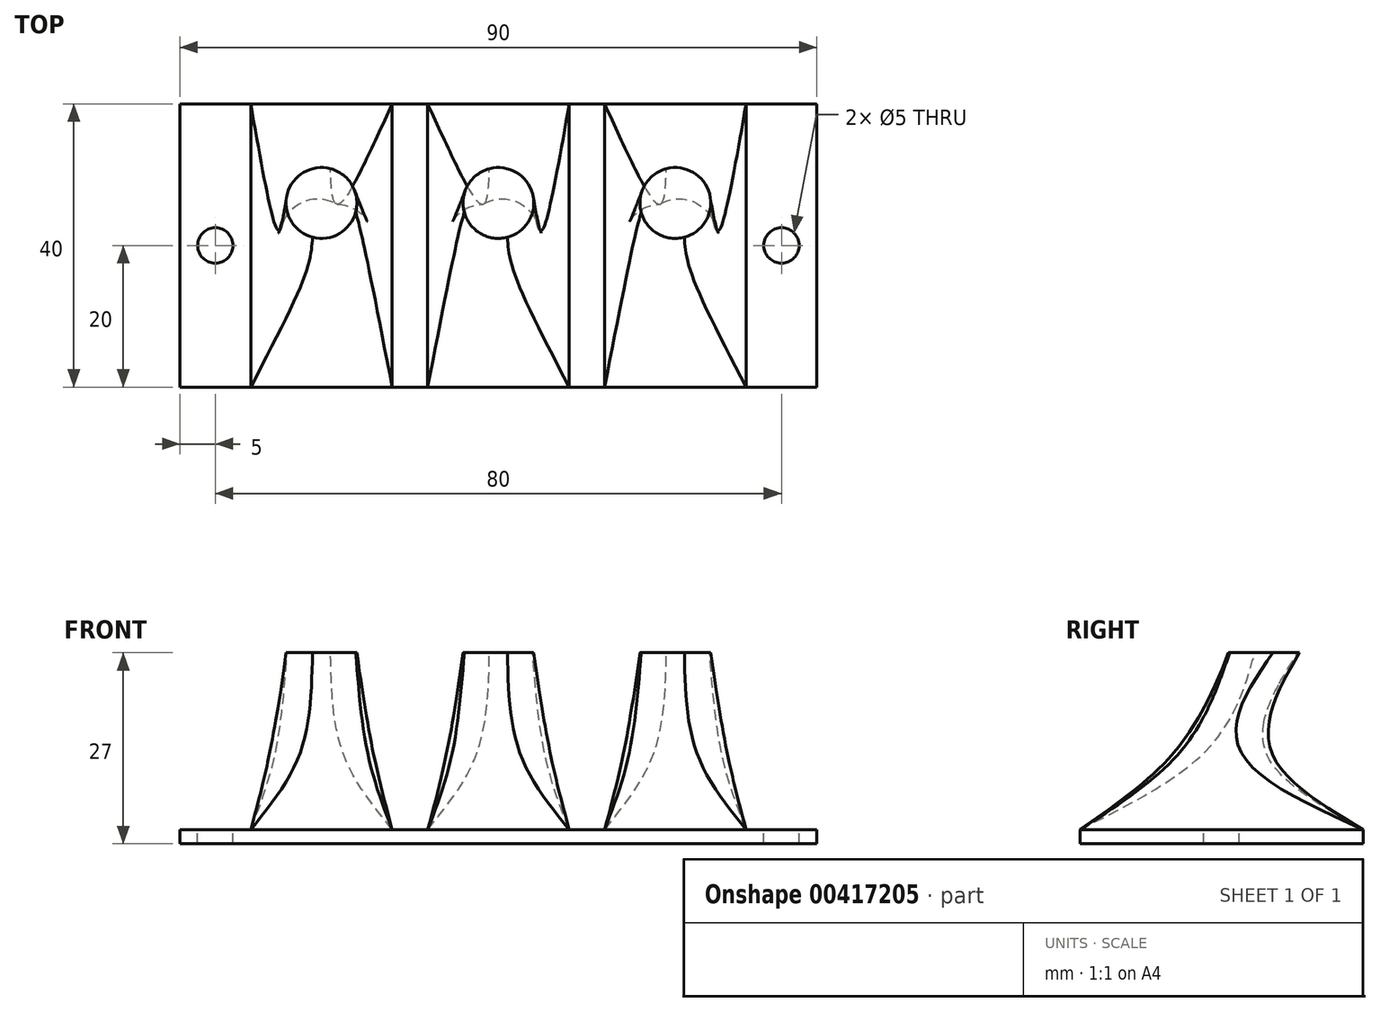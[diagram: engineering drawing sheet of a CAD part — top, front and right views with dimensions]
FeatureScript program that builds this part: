
annotation { "Feature Type Name" : "Feature", "Feature Type Description" : "" }
export const myFeature = defineFeature(function(context is Context, id is Id, definition is map)
    precondition{}
    {
        {
            var Q0;
            Q0=qCreatedBy(makeId("Top.planeOp"),FACE);
            var sketch = newSketch(context, id + "F0", { "sketchPlane" : qUnion([Q0])});
            skLineSegment(sketch, "E0.bottom", {"start": v(10, -20) * mm, "end": v(-10, -20) * mm});
            skLineSegment(sketch, "E0.top", {"start": v(10, 20) * mm, "end": v(-10, 20) * mm});
            skLineSegment(sketch, "E0.left", {"start": v(10, -20) * mm, "end": v(10, 20) * mm});
            skLineSegment(sketch, "E0.right", {"start": v(-10, -20) * mm, "end": v(-10, 20) * mm});
            skPoint(sketch, "E0.middle", {"position": v(0, 0) * mm});
            skSolve(sketch);
        }
        {
            var Q0;
            Q0=qCreatedBy(makeId("Top.planeOp"),FACE);
            cPlane(context, id + "F1", {"entities" : qUnion([Q0]), "cplaneType" : CPlaneType.OFFSET, "offset" : 25 * mm, "width" : 150 * mm, "height" : 150 * mm});
        }
        {
            var Q0;
            Q0=qCreatedBy(id+"F1.planeOp",FACE);
            var sketch = newSketch(context, id + "F2", { "sketchPlane" : qUnion([Q0])});
            skCircle(sketch, "E1", {"center": v(0, 6) * mm, "radius": 5 * mm});
            skSolve(sketch);
        }
        {
            var Q0;
            Q0=qCreatedBy(makeId("Top.planeOp"),FACE);
            cPlane(context, id + "F3", {"entities" : qUnion([Q0]), "cplaneType" : CPlaneType.OFFSET, "offset" : 10 * mm, "width" : 150 * mm, "height" : 150 * mm});
        }
        {
            var Q0;
            Q0=qCreatedBy(id+"F3.planeOp",FACE);
            var sketch = newSketch(context, id + "F4", { "sketchPlane" : qUnion([Q0])});
            skCircle(sketch, "E2", {"center": v(0, 0) * mm, "radius": 7.5 * mm});
            skSolve(sketch);
        }
        {
            var Q0;
            Q0=makeQuery(id+"F0.imprint","IMPRINT",FACE,{"disambiguationData":[TD([[makeQuery(id+"F0.imprint","IMPRINT",EDGE,{"derivedFrom":sQuery(id+"F0.wireOp",EDGE,"E0.bottom")}),-1.0]])]});
            var Q1;
            Q1=makeQuery(id+"F4.imprint","IMPRINT",FACE,{"disambiguationData":[TD([[makeQuery(id+"F4.imprint","IMPRINT",EDGE,{"derivedFrom":sQuery(id+"F4.wireOp",EDGE,"E2")}),1.0]])]});
            var Q2;
            Q2=makeQuery(id+"F2.imprint","IMPRINT",FACE,{"disambiguationData":[TD([[makeQuery(id+"F2.imprint","IMPRINT",EDGE,{"derivedFrom":sQuery(id+"F2.wireOp",EDGE,"E1")}),1.0]])]});
            loft(context, id + "F5", {"sheetProfilesArray" : [{ "sheetProfileEntities" : qUnion([Q0]) }, { "sheetProfileEntities" : qUnion([Q1]) }, { "sheetProfileEntities" : qUnion([Q2]) }]});
        }
        {
            var Q0;
            Q0=qCreatedBy(makeId("Top.planeOp"),FACE);
            var sketch = newSketch(context, id + "F6", { "sketchPlane" : qUnion([Q0])});
            skLineSegment(sketch, "E3", {"start": v(0, 0) * mm, "end": v(25, 0) * mm});
            skLineSegment(sketch, "E4.bottom", {"start": v(35, -20) * mm, "end": v(15, -20) * mm});
            skLineSegment(sketch, "E4.top", {"start": v(35, 20) * mm, "end": v(15, 20) * mm});
            skLineSegment(sketch, "E4.left", {"start": v(35, -20) * mm, "end": v(35, 20) * mm});
            skLineSegment(sketch, "E4.right", {"start": v(15, -20) * mm, "end": v(15, 20) * mm});
            skPoint(sketch, "E4.middle", {"position": v(25, 0) * mm});
            skSolve(sketch);
        }
        {
            var Q0;
            Q0=qCreatedBy(makeId("Top.planeOp"),FACE);
            cPlane(context, id + "F7", {"entities" : qUnion([Q0]), "cplaneType" : CPlaneType.OFFSET, "offset" : 10 * mm, "width" : 150 * mm, "height" : 150 * mm});
        }
        {
            var Q0;
            Q0=qCreatedBy(id+"F7.planeOp",FACE);
            var sketch = newSketch(context, id + "F8", { "sketchPlane" : qUnion([Q0])});
            skLineSegment(sketch, "E5", {"start": v(0, 0) * mm, "end": v(25, 0) * mm});
            skCircle(sketch, "E6", {"center": v(25, 0) * mm, "radius": 7.5 * mm});
            skSolve(sketch);
        }
        {
            var Q0;
            Q0=qCreatedBy(makeId("Top.planeOp"),FACE);
            cPlane(context, id + "F9", {"entities" : qUnion([Q0]), "cplaneType" : CPlaneType.OFFSET, "offset" : 25 * mm, "width" : 150 * mm, "height" : 150 * mm});
        }
        {
            var Q0;
            Q0=qCreatedBy(id+"F9.planeOp",FACE);
            var sketch = newSketch(context, id + "F10", { "sketchPlane" : qUnion([Q0])});
            skLineSegment(sketch, "E7", {"start": v(0, 0) * mm, "end": v(25, 0) * mm});
            skLineSegment(sketch, "E8", {"start": v(25, 0) * mm, "end": v(25, 6) * mm});
            skCircle(sketch, "E9", {"center": v(25, 6) * mm, "radius": 5 * mm});
            skSolve(sketch);
        }
        {
            var Q0;
            {var subQ0=sQuery(id+"F6.wireOp",EDGE,"E4.bottom");Q0=makeQuery(id+"F6.imprint","IMPRINT",FACE,{"disambiguationData":[TD([[makeQuery(id+"F6.imprint","IMPRINT",EDGE,{"derivedFrom":subQ0}),-1.0]])]});}
            var Q1;
            Q1=makeQuery(id+"F8.imprint","IMPRINT",FACE,{"disambiguationData":[TD([[makeQuery(id+"F8.imprint","IMPRINT",EDGE,{"derivedFrom":sQuery(id+"F8.wireOp",EDGE,"E6")}),1.0]])]});
            var Q2;
            Q2=makeQuery(id+"F10.imprint","IMPRINT",FACE,{"disambiguationData":[TD([[makeQuery(id+"F10.imprint","IMPRINT",EDGE,{"derivedFrom":sQuery(id+"F10.wireOp",EDGE,"E9")}),1.0]])]});
            loft(context, id + "F11", {"sheetProfilesArray" : [{ "sheetProfileEntities" : qUnion([Q0]) }, { "sheetProfileEntities" : qUnion([Q1]) }, { "sheetProfileEntities" : qUnion([Q2]) }]});
        }
        {
            var Q0;
            Q0=qCreatedBy(makeId("Top.planeOp"),FACE);
            var sketch = newSketch(context, id + "F12", { "sketchPlane" : qUnion([Q0])});
            skLineSegment(sketch, "E10", {"start": v(0, 0) * mm, "end": v(-25, 0) * mm});
            skLineSegment(sketch, "E11.bottom", {"start": v(-35, -20) * mm, "end": v(-15, -20) * mm});
            skLineSegment(sketch, "E11.top", {"start": v(-35, 20) * mm, "end": v(-15, 20) * mm});
            skLineSegment(sketch, "E11.left", {"start": v(-35, -20) * mm, "end": v(-35, 20) * mm});
            skLineSegment(sketch, "E11.right", {"start": v(-15, -20) * mm, "end": v(-15, 20) * mm});
            skPoint(sketch, "E11.middle", {"position": v(-25, 0) * mm});
            skSolve(sketch);
        }
        {
            var Q0;
            Q0=qCreatedBy(makeId("Top.planeOp"),FACE);
            cPlane(context, id + "F13", {"entities" : qUnion([Q0]), "cplaneType" : CPlaneType.OFFSET, "offset" : 10 * mm, "width" : 150 * mm, "height" : 150 * mm});
        }
        {
            var Q0;
            Q0=qCreatedBy(id+"F13.planeOp",FACE);
            var sketch = newSketch(context, id + "F14", { "sketchPlane" : qUnion([Q0])});
            skLineSegment(sketch, "E12", {"start": v(0, 0) * mm, "end": v(-25, 0) * mm});
            skCircle(sketch, "E13", {"center": v(-25, 0) * mm, "radius": 7.5 * mm});
            skSolve(sketch);
        }
        {
            var Q0;
            Q0=qCreatedBy(makeId("Top.planeOp"),FACE);
            cPlane(context, id + "F15", {"entities" : qUnion([Q0]), "cplaneType" : CPlaneType.OFFSET, "offset" : 25 * mm, "width" : 150 * mm, "height" : 150 * mm});
        }
        {
            var Q0;
            Q0=qCreatedBy(id+"F15.planeOp",FACE);
            var sketch = newSketch(context, id + "F16", { "sketchPlane" : qUnion([Q0])});
            skLineSegment(sketch, "E14", {"start": v(0, 0) * mm, "end": v(-25, 0) * mm});
            skLineSegment(sketch, "E15", {"start": v(-25, 0) * mm, "end": v(-25, 6) * mm});
            skCircle(sketch, "E16", {"center": v(-25, 6) * mm, "radius": 5 * mm});
            skSolve(sketch);
        }
        {
            var Q0;
            {var subQ0=sQuery(id+"F12.wireOp",EDGE,"E11.bottom");Q0=makeQuery(id+"F12.imprint","IMPRINT",FACE,{"disambiguationData":[TD([[makeQuery(id+"F12.imprint","IMPRINT",EDGE,{"derivedFrom":subQ0}),1.0]])]});}
            var Q1;
            Q1=makeQuery(id+"F14.imprint","IMPRINT",FACE,{"disambiguationData":[TD([[makeQuery(id+"F14.imprint","IMPRINT",EDGE,{"derivedFrom":sQuery(id+"F14.wireOp",EDGE,"E13")}),1.0]])]});
            var Q2;
            Q2=makeQuery(id+"F16.imprint","IMPRINT",FACE,{"disambiguationData":[TD([[makeQuery(id+"F16.imprint","IMPRINT",EDGE,{"derivedFrom":sQuery(id+"F16.wireOp",EDGE,"E16")}),1.0]])]});
            loft(context, id + "F17", {"sheetProfilesArray" : [{ "sheetProfileEntities" : qUnion([Q0]) }, { "sheetProfileEntities" : qUnion([Q1]) }, { "sheetProfileEntities" : qUnion([Q2]) }]});
        }
        {
            var Q0;
            Q0=qCreatedBy(makeId("Top.planeOp"),FACE);
            var sketch = newSketch(context, id + "F18", { "sketchPlane" : qUnion([Q0])});
            skLineSegment(sketch, "E17.bottom", {"start": v(45, -20) * mm, "end": v(-45, -20) * mm});
            skLineSegment(sketch, "E17.top", {"start": v(45, 20) * mm, "end": v(-45, 20) * mm});
            skLineSegment(sketch, "E17.left", {"start": v(45, -20) * mm, "end": v(45, 20) * mm});
            skLineSegment(sketch, "E17.right", {"start": v(-45, -20) * mm, "end": v(-45, 20) * mm});
            skPoint(sketch, "E17.middle", {"position": v(0, 0) * mm});
            skSolve(sketch);
        }
        {
            var Q0;
            Q0=qSketchRegion(id+"F18",true);
            extrude(context, id + "F19", {"entities" : qUnion([Q0]), "oppositeDirection" : true, "depth" : 2 * mm, "offsetDistance" : 25 * mm});
        }
        {
            var Q0;
            Q0=makeQuery(id+"F19.opExtrude","CAP_FACE",FACE,{"disambiguationData":[OSD([sQuery(id+"F18.wireOp",EDGE,"E17.bottom"),sQuery(id+"F18.wireOp",EDGE,"E17.top"),sQuery(id+"F18.wireOp",EDGE,"E17.left"),sQuery(id+"F18.wireOp",EDGE,"E17.right")])],"isStart":true});
            var sketch = newSketch(context, id + "F20", { "sketchPlane" : qUnion([Q0])});
            skLineSegment(sketch, "E18", {"start": v(45, 0) * mm, "end": v(40, 0) * mm});
            skLineSegment(sketch, "E19", {"start": v(-45, 0) * mm, "end": v(-40, 0) * mm});
            skSolve(sketch);
        }
        {
            var Q0;
            Q0=sQuery(id+"F20.wireOp",VERTEX,"E18.end");
            var Q1;
            Q1=sQuery(id+"F20.wireOp",VERTEX,"E19.end");
            var Q2;
            Q2=makeQuery(id+"F19.opExtrude","SWEPT_BODY",BODY,{"disambiguationData":[OSD([sQuery(id+"F18.wireOp",EDGE,"E17.bottom"),sQuery(id+"F18.wireOp",EDGE,"E17.top"),sQuery(id+"F18.wireOp",EDGE,"E17.left"),sQuery(id+"F18.wireOp",EDGE,"E17.right")])]});
            hole(context, id + "F21", {"style" : HoleStyle.C_BORE, "endStyle" : HoleEndStyle.BLIND, "holeDiameter" : 5 * mm, "cBoreDiameter" : 5 * mm, "cBoreDepth" : 2 * mm, "holeDepth" : 8 * mm, "isTappedThrough" : true, "tappedDepth" : 12 * mm, "tapClearance" : 3, "locations" : qUnion([Q0, Q1]), "scope" : qUnion([Q2])});
        }
    });
